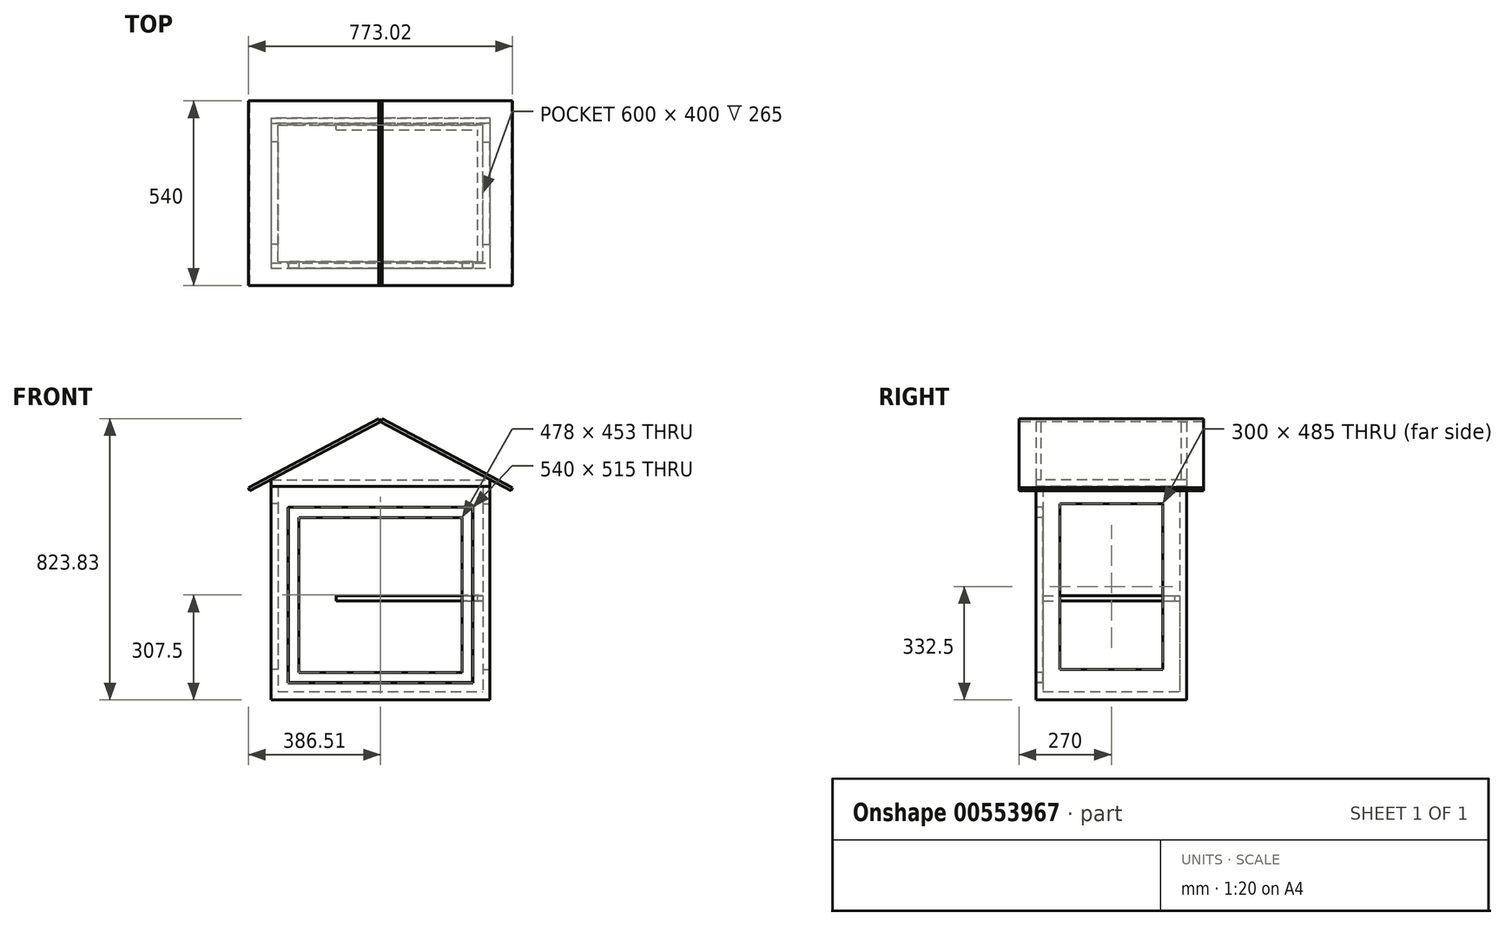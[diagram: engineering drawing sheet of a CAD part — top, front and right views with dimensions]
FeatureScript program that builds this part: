
annotation { "Feature Type Name" : "Feature", "Feature Type Description" : "" }
export const myFeature = defineFeature(function(context is Context, id is Id, definition is map)
    precondition{}
    {
        {
            var Q0;
            Q0=qCreatedBy(makeId("Top.planeOp"),FACE);
            var sketch = newSketch(context, id + "F0", { "sketchPlane" : qUnion([Q0])});
            skLineSegment(sketch, "E0.bottom", {"start": v(-300, -200) * mm, "end": v(300, -200) * mm});
            skLineSegment(sketch, "E0.top", {"start": v(-300, 200) * mm, "end": v(300, 200) * mm});
            skLineSegment(sketch, "E0.left", {"start": v(-300, -200) * mm, "end": v(-300, 200) * mm});
            skLineSegment(sketch, "E0.right", {"start": v(300, -200) * mm, "end": v(300, 200) * mm});
            skLineSegment(sketch, "E1.bottom", {"start": v(-320, 220) * mm, "end": v(320, 220) * mm});
            skLineSegment(sketch, "E1.top", {"start": v(-320, -220) * mm, "end": v(320, -220) * mm});
            skLineSegment(sketch, "E1.left", {"start": v(-320, 220) * mm, "end": v(-320, -220) * mm});
            skLineSegment(sketch, "E1.right", {"start": v(320, 220) * mm, "end": v(320, -220) * mm});
            skSolve(sketch);
        }
        {
            var Q0;
            Q0 = qSketchRegion(id + "F0", true);
            extrude(context, id + "F1", {"entities" : qUnion([Q0]), "depth" : 600 * mm, "offsetDistance" : 25 * mm});
        }
        {
            var Q0;
            Q0=makeQuery(id+"F1.opExtrude","CAP_FACE",FACE,{"disambiguationData":[OSD([sQuery(id+"F0.wireOp",EDGE,"E0.bottom"),sQuery(id+"F0.wireOp",EDGE,"E0.top"),sQuery(id+"F0.wireOp",EDGE,"E0.left"),sQuery(id+"F0.wireOp",EDGE,"E0.right"),sQuery(id+"F0.wireOp",EDGE,"E1.bottom"),sQuery(id+"F0.wireOp",EDGE,"E1.top"),sQuery(id+"F0.wireOp",EDGE,"E1.left"),sQuery(id+"F0.wireOp",EDGE,"E1.right")])],"isStart":false});
            var sketch = newSketch(context, id + "F2", { "sketchPlane" : qUnion([Q0])});
            skLineSegment(sketch, "E2.bottom", {"start": v(320, -220) * mm, "end": v(-320, -220) * mm});
            skLineSegment(sketch, "E2.top", {"start": v(320, 220) * mm, "end": v(-320, 220) * mm});
            skLineSegment(sketch, "E2.left", {"start": v(320, -220) * mm, "end": v(320, 220) * mm});
            skLineSegment(sketch, "E2.right", {"start": v(-320, -220) * mm, "end": v(-320, 220) * mm});
            skSolve(sketch);
        }
        {
            var Q0;
            Q0 = qSketchRegion(id + "F2", true);
            extrude(context, id + "F3", {"entities" : qUnion([Q0]), "depth" : 20 * mm, "offsetDistance" : 25 * mm});
        }
        {
            var Q0;
            Q0=makeQuery(id+"F1.opExtrude","SWEPT_FACE",FACE,{"disambiguationData":[OSD([sQuery(id+"F0.wireOp",EDGE,"E1.right")])]});
            var sketch = newSketch(context, id + "F4", { "sketchPlane" : qUnion([Q0])});
            skLineSegment(sketch, "E3.bottom", {"start": v(-150, 550) * mm, "end": v(150, 550) * mm});
            skLineSegment(sketch, "E3.top", {"start": v(-150, 65) * mm, "end": v(150, 65) * mm});
            skLineSegment(sketch, "E3.left", {"start": v(-150, 550) * mm, "end": v(-150, 65) * mm});
            skLineSegment(sketch, "E3.right", {"start": v(150, 550) * mm, "end": v(150, 65) * mm});
            skSolve(sketch);
        }
        {
            var Q0;
            Q0 = qSketchRegion(id + "F4", true);
            extrude(context, id + "F5", {"entities" : qUnion([Q0]), "operationType" : NewBodyOperationType.REMOVE, "oppositeDirection" : true, "depth" : 20 * mm, "offsetDistance" : 25 * mm});
        }
        {
            var Q0;
            Q0=makeQuery(id+"F1.opExtrude","SWEPT_FACE",FACE,{"disambiguationData":[OSD([sQuery(id+"F0.wireOp",EDGE,"E1.top")])]});
            var sketch = newSketch(context, id + "F6", { "sketchPlane" : qUnion([Q0])});
            skLineSegment(sketch, "E4.bottom", {"start": v(270, 25) * mm, "end": v(-270, 25) * mm});
            skLineSegment(sketch, "E4.top", {"start": v(270, 540) * mm, "end": v(-270, 540) * mm});
            skLineSegment(sketch, "E4.left", {"start": v(270, 25) * mm, "end": v(270, 540) * mm});
            skLineSegment(sketch, "E4.right", {"start": v(-270, 25) * mm, "end": v(-270, 540) * mm});
            skSolve(sketch);
        }
        {
            var Q0;
            Q0 = qSketchRegion(id + "F6", true);
            extrude(context, id + "F7", {"entities" : qUnion([Q0]), "operationType" : NewBodyOperationType.REMOVE, "oppositeDirection" : true, "depth" : 20 * mm, "offsetDistance" : 25 * mm});
        }
        {
            var Q0;
            Q0=makeQuery(id+"F1.opExtrude","SWEPT_FACE",FACE,{"disambiguationData":[OSD([sQuery(id+"F0.wireOp",EDGE,"E1.left")])]});
            var sketch = newSketch(context, id + "F8", { "sketchPlane" : qUnion([Q0])});
            skLineSegment(sketch, "E5.bottom", {"start": v(-150, 550) * mm, "end": v(150, 550) * mm});
            skLineSegment(sketch, "E5.top", {"start": v(-150, 65) * mm, "end": v(150, 65) * mm});
            skLineSegment(sketch, "E5.left", {"start": v(-150, 550) * mm, "end": v(-150, 65) * mm});
            skLineSegment(sketch, "E5.right", {"start": v(150, 550) * mm, "end": v(150, 65) * mm});
            skSolve(sketch);
        }
        {
            var Q0;
            Q0 = qSketchRegion(id + "F8", true);
            extrude(context, id + "F9", {"entities" : qUnion([Q0]), "operationType" : NewBodyOperationType.REMOVE, "endBound" : BoundingType.THROUGH_ALL, "oppositeDirection" : true, "depth" : 20 * mm, "offsetDistance" : 25 * mm});
        }
        {
            var Q0;
            Q0=makeQuery(id+"F1.opExtrude","CAP_FACE",FACE,{"disambiguationData":[OSD([sQuery(id+"F0.wireOp",EDGE,"E0.bottom"),sQuery(id+"F0.wireOp",EDGE,"E0.top"),sQuery(id+"F0.wireOp",EDGE,"E0.left"),sQuery(id+"F0.wireOp",EDGE,"E0.right"),sQuery(id+"F0.wireOp",EDGE,"E1.bottom"),sQuery(id+"F0.wireOp",EDGE,"E1.top"),sQuery(id+"F0.wireOp",EDGE,"E1.left"),sQuery(id+"F0.wireOp",EDGE,"E1.right")])],"isStart":true});
            var sketch = newSketch(context, id + "F10", { "sketchPlane" : qUnion([Q0])});
            skLineSegment(sketch, "E6.bottom", {"start": v(320, 220) * mm, "end": v(-320, 220) * mm});
            skLineSegment(sketch, "E6.top", {"start": v(320, -220) * mm, "end": v(-320, -220) * mm});
            skLineSegment(sketch, "E6.left", {"start": v(320, 220) * mm, "end": v(320, -220) * mm});
            skLineSegment(sketch, "E6.right", {"start": v(-320, 220) * mm, "end": v(-320, -220) * mm});
            skSolve(sketch);
        }
        {
            var Q0;
            Q0 = qSketchRegion(id + "F10", true);
            extrude(context, id + "F11", {"entities" : qUnion([Q0]), "operationType" : NewBodyOperationType.ADD, "depth" : 25 * mm, "offsetDistance" : 25 * mm});
        }
        {
            var Q0;
            Q0=makeQuery(id+"F1.opExtrude","SWEPT_FACE",FACE,{"disambiguationData":[OSD([sQuery(id+"F0.wireOp",EDGE,"E0.top")])]});
            var sketch = newSketch(context, id + "F12", { "sketchPlane" : qUnion([Q0])});
            skPoint(sketch, "E7.oppositeSnap0", {"position": v(300, 300) * mm});
            skLineSegment(sketch, "E7.bottom", {"start": v(300, 280) * mm, "end": v(-150, 280) * mm});
            skLineSegment(sketch, "E7.top", {"start": v(300, 300) * mm, "end": v(-150, 300) * mm});
            skLineSegment(sketch, "E7.left", {"start": v(300, 280) * mm, "end": v(300, 300) * mm});
            skLineSegment(sketch, "E7.right", {"start": v(-150, 280) * mm, "end": v(-150, 300) * mm});
            skLineSegment(sketch, "E8.bottom", {"start": v(-150, 280) * mm, "end": v(-130, 280) * mm});
            skLineSegment(sketch, "E8.top", {"start": v(-150, 0) * mm, "end": v(-130, 0) * mm});
            skLineSegment(sketch, "E8.left", {"start": v(-150, 280) * mm, "end": v(-150, 0) * mm});
            skLineSegment(sketch, "E8.right", {"start": v(-130, 280) * mm, "end": v(-130, 0) * mm});
            skSolve(sketch);
        }
        {
            var Q0;
            Q0=makeQuery(id+"Faog9uu1IL17dyW_2.boolean.opBoolean","SPLIT",FACE,{"disambiguationData":[TD([makeQuery(id+"Faog9uu1IL17dyW_2.opExtrude","SWEPT_FACE",FACE,{"disambiguationData":[OSD([sQuery(id+"F12.wireOp",EDGE,"E7.bottom")])]})])],"derivedFrom":makeQuery(id+"F1.opExtrude","SWEPT_FACE",FACE,{"disambiguationData":[OSD([sQuery(id+"F0.wireOp",EDGE,"E0.top")])]})});
            var sketch = newSketch(context, id + "F13", { "sketchPlane" : qUnion([Q0])});
            skLineSegment(sketch, "E9.bottom", {"start": v(300, 280) * mm, "end": v(285, 280) * mm});
            skLineSegment(sketch, "E9.top", {"start": v(300, 265) * mm, "end": v(285, 265) * mm});
            skLineSegment(sketch, "E9.left", {"start": v(300, 280) * mm, "end": v(300, 265) * mm});
            skLineSegment(sketch, "E9.right", {"start": v(285, 280) * mm, "end": v(285, 265) * mm});
            skSolve(sketch);
        }
        {
            var Q0;
            Q0 = qSketchRegion(id + "F13", true);
            var Q1;
            Q1=makeQuery(id+"F1.opExtrude","SWEPT_FACE",FACE,{"disambiguationData":[OSD([sQuery(id+"F0.wireOp",EDGE,"E0.bottom")])]});
            extrude(context, id + "F14", {"entities" : qUnion([Q0]), "operationType" : NewBodyOperationType.ADD, "endBound" : BoundingType.UP_TO_SURFACE, "depth" : 25 * mm, "endBoundEntityFace" : qUnion([Q1]), "offsetDistance" : 25 * mm});
        }
        {
            var Q0;
            Q0=makeQuery(id+"Faog9uu1IL17dyW_2.boolean.opBoolean","SPLIT",FACE,{"disambiguationData":[TD([makeQuery(id+"Faog9uu1IL17dyW_2.opExtrude","SWEPT_FACE",FACE,{"disambiguationData":[OSD([sQuery(id+"F12.wireOp",EDGE,"E7.bottom")])]})])],"derivedFrom":makeQuery(id+"F1.opExtrude","SWEPT_FACE",FACE,{"disambiguationData":[OSD([sQuery(id+"F0.wireOp",EDGE,"E0.top")])]})});
            var sketch = newSketch(context, id + "F15", { "sketchPlane" : qUnion([Q0])});
            skLineSegment(sketch, "E10.bottom", {"start": v(-130, 280) * mm, "end": v(285, 280) * mm});
            skLineSegment(sketch, "E10.top", {"start": v(-130, 265) * mm, "end": v(285, 265) * mm});
            skLineSegment(sketch, "E10.left", {"start": v(-130, 280) * mm, "end": v(-130, 265) * mm});
            skLineSegment(sketch, "E10.right", {"start": v(285, 280) * mm, "end": v(285, 265) * mm});
            skSolve(sketch);
        }
        {
            var Q0;
            Q0 = qSketchRegion(id + "F15", true);
            extrude(context, id + "F16", {"entities" : qUnion([Q0]), "operationType" : NewBodyOperationType.ADD, "depth" : 15 * mm, "offsetDistance" : 25 * mm});
        }
        {
            var Q0;
            Q0=makeQuery(id+"F3.opExtrude","SWEPT_FACE",FACE,{"disambiguationData":[OSD([sQuery(id+"F2.wireOp",EDGE,"E2.bottom")])]});
            var sketch = newSketch(context, id + "F17", { "sketchPlane" : qUnion([Q0])});
            skLineSegment(sketch, "E11", {"start": v(-320, 620) * mm, "end": v(0, 790) * mm});
            skPoint(sketch, "E11.endSnap0", {"position": v(0, 620) * mm});
            skLineSegment(sketch, "E12", {"start": v(0, 790) * mm, "end": v(320, 620) * mm});
            skSolve(sketch);
        }
        {
            var Q0;
            Q0=makeQuery(id+"F17.imprint","IMPRINT",FACE,{"disambiguationData":[TD([[makeQuery(id+"F17.imprint","IMPRINT",EDGE,{"derivedFrom":sQuery(id+"F17.wireOp",EDGE,"E11")}),-1.0]])]});
            extrude(context, id + "F18", {"entities" : qUnion([Q0]), "operationType" : NewBodyOperationType.ADD, "oppositeDirection" : true, "depth" : 15 * mm, "offsetDistance" : 25 * mm});
        }
        {
            var Q0;
            Q0=makeQuery(id+"F3.opExtrude","SWEPT_FACE",FACE,{"disambiguationData":[OSD([sQuery(id+"F2.wireOp",EDGE,"E2.top")])]});
            var sketch = newSketch(context, id + "F19", { "sketchPlane" : qUnion([Q0])});
            skLineSegment(sketch, "E13", {"start": v(-320, 620) * mm, "end": v(0, 790) * mm});
            skLineSegment(sketch, "E14", {"start": v(0, 790) * mm, "end": v(320, 620) * mm});
            skLineSegment(sketch, "E15", {"start": v(320, 620) * mm, "end": v(-320, 620) * mm});
            skSolve(sketch);
        }
        {
            var Q0;
            Q0 = qSketchRegion(id + "F19", true);
            extrude(context, id + "F20", {"entities" : qUnion([Q0]), "operationType" : NewBodyOperationType.ADD, "oppositeDirection" : true, "depth" : 15 * mm, "offsetDistance" : 25 * mm});
        }
        {
            var Q0;
            Q0=makeQuery(id+"F18.opExtrude","SWEPT_FACE",FACE,{"disambiguationData":[OSD([sQuery(id+"F17.wireOp",EDGE,"E11")])]});
            var sketch = newSketch(context, id + "F21", { "sketchPlane" : qUnion([Q0])});
            skLineSegment(sketch, "E16.bottom", {"start": v(370.63, -270) * mm, "end": v(-61.72, -270) * mm});
            skLineSegment(sketch, "E16.top", {"start": v(370.63, 270) * mm, "end": v(-61.72, 270) * mm});
            skLineSegment(sketch, "E16.left", {"start": v(370.63, -270) * mm, "end": v(370.63, 270) * mm});
            skLineSegment(sketch, "E16.right", {"start": v(-61.72, -270) * mm, "end": v(-61.72, 270) * mm});
            skSolve(sketch);
        }
        {
            var Q0;
            Q0=makeQuery(id+"F20.opExtrude","SWEPT_FACE",FACE,{"disambiguationData":[OSD([sQuery(id+"F19.wireOp",EDGE,"E13")])]});
            var sketch = newSketch(context, id + "F22", { "sketchPlane" : qUnion([Q0])});
            skLineSegment(sketch, "E17.bottom", {"start": v(-370.63, 270) * mm, "end": v(61.72, 270) * mm});
            skLineSegment(sketch, "E17.top", {"start": v(-370.63, -270) * mm, "end": v(61.72, -270) * mm});
            skLineSegment(sketch, "E17.left", {"start": v(-370.63, 270) * mm, "end": v(-370.63, -270) * mm});
            skLineSegment(sketch, "E17.right", {"start": v(61.72, 270) * mm, "end": v(61.72, -270) * mm});
            skSolve(sketch);
        }
        {
            var Q0;
            Q0 = qSketchRegion(id + "F21", true);
            extrude(context, id + "F23", {"entities" : qUnion([Q0]), "depth" : 10 * mm, "offsetDistance" : 25 * mm});
        }
        {
            var Q0;
            Q0 = qSketchRegion(id + "F22", true);
            extrude(context, id + "F24", {"entities" : qUnion([Q0]), "depth" : 10 * mm, "offsetDistance" : 25 * mm});
        }
        {
            var Q0;
            Q0=makeQuery(id+"F11.boolean.opBoolean","MERGE",FACE,{"derivedFrom":[makeQuery(id+"F1.opExtrude","SWEPT_FACE",FACE,{"disambiguationData":[OSD([sQuery(id+"F0.wireOp",EDGE,"E1.top")])]}),makeQuery(id+"F11.opExtrude","SWEPT_FACE",FACE,{"disambiguationData":[OSD([sQuery(id+"F10.wireOp",EDGE,"E6.bottom")])]})]});
            var sketch = newSketch(context, id + "F25", { "sketchPlane" : qUnion([Q0])});
            skLineSegment(sketch, "E18.bottom", {"start": v(-269, 539) * mm, "end": v(269, 539) * mm});
            skLineSegment(sketch, "E18.top", {"start": v(-269, 26) * mm, "end": v(269, 26) * mm});
            skLineSegment(sketch, "E18.left", {"start": v(-269, 539) * mm, "end": v(-269, 26) * mm});
            skLineSegment(sketch, "E18.right", {"start": v(269, 539) * mm, "end": v(269, 26) * mm});
            skLineSegment(sketch, "E19.bottom", {"start": v(-239, 509) * mm, "end": v(239, 509) * mm});
            skLineSegment(sketch, "E19.top", {"start": v(-239, 56) * mm, "end": v(239, 56) * mm});
            skLineSegment(sketch, "E19.left", {"start": v(-239, 509) * mm, "end": v(-239, 56) * mm});
            skLineSegment(sketch, "E19.right", {"start": v(239, 509) * mm, "end": v(239, 56) * mm});
            skSolve(sketch);
        }
        {
            var Q0;
            Q0 = qSketchRegion(id + "F25", true);
            extrude(context, id + "F26", {"entities" : qUnion([Q0]), "oppositeDirection" : true, "depth" : 20 * mm, "offsetDistance" : 25 * mm});
        }
    });
